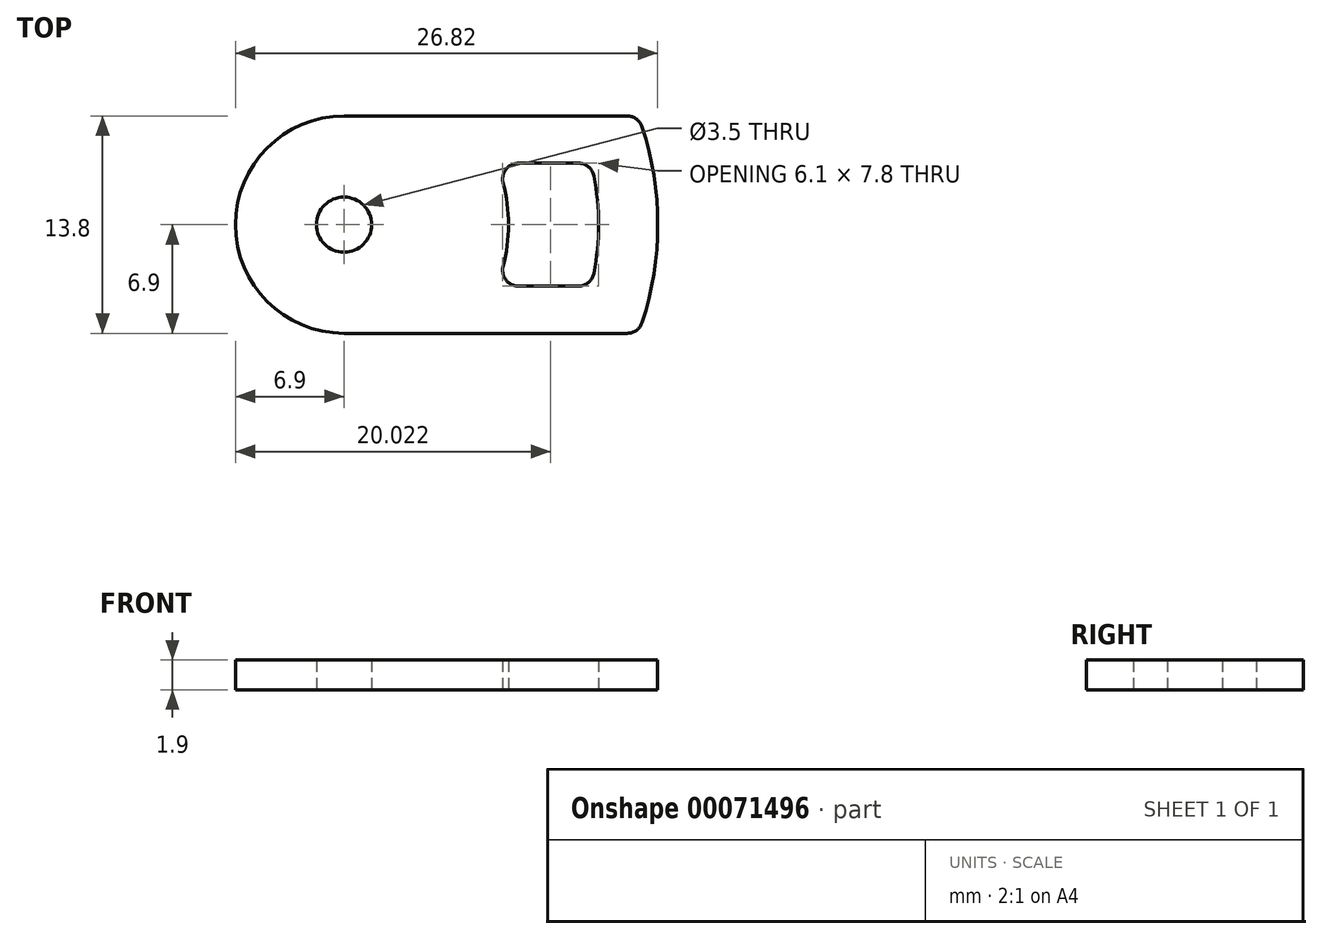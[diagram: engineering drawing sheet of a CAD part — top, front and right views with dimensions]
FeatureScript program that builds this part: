
annotation { "Feature Type Name" : "Feature", "Feature Type Description" : "" }
export const myFeature = defineFeature(function(context is Context, id is Id, definition is map)
    precondition{}
    {
        {
            var Q0;
            Q0=qCreatedBy(makeId("Top.planeOp"),FACE);
            var sketch = newSketch(context, id + "F0", { "sketchPlane" : qUnion([Q0])});
            skCircle(sketch, "E0", {"center": v(0, 0) * mm, "radius": 1.75 * mm});
            skCircle(sketch, "E1", {"center": v(0, 0) * mm, "radius": 6.9 * mm});
            skLineSegment(sketch, "E2", {"start": v(0, 6.9) * mm, "end": v(18.7, 6.9) * mm});
            skLineSegment(sketch, "E3", {"start": v(0, -6.9) * mm, "end": v(18.7, -6.9) * mm});
            skLineSegment(sketch, "E4", {"start": v(9.7, 3.9) * mm, "end": v(15.7, 3.9) * mm});
            skLineSegment(sketch, "E5", {"start": v(15.7, -3.9) * mm, "end": v(9.7, -3.9) * mm});
            skLineSegment(sketch, "E6", {"start": v(9.7, 3.9) * mm, "end": v(5.7, 3.9) * mm, "construction": true});
            skLineSegment(sketch, "E7", {"start": v(5.7, 3.9) * mm, "end": v(5.7, 6.9) * mm, "construction": true});
            skCircle(sketch, "E8", {"center": v(0, 0) * mm, "radius": 10.45 * mm});
            skCircle(sketch, "E9", {"center": v(0, 0) * mm, "radius": 19.92 * mm});
            skCircle(sketch, "E10", {"center": v(0, 0) * mm, "radius": 16.17 * mm});
            skSolve(sketch);
        }
        {
            var Q0;
            Q0=makeQuery(id+"F0.imprint","IMPRINT",FACE,{"disambiguationData":[TD([[makeQuery(id+"F0.imprint","IMPRINT",EDGE,{"derivedFrom":sQuery(id+"F0.wireOp",EDGE,"E0")}),-1.0]])]});
            var Q1;
            {var subQ2=sQuery(id+"F0.wireOp",EDGE,"E2");var subQ5=sQuery(id+"F0.wireOp",EDGE,"E1");var subQ9=makeQuery(id+"F0.imprint","INTERSECT",VERTEX,{"derivedFrom":[subQ5,subQ2]});Q1=makeQuery(id+"F0.imprint","IMPRINT",FACE,{"disambiguationData":[TD([[makeQuery(id+"F0.imprint","IMPRINT",EDGE,{"disambiguationData":[TD([[subQ9,1.0]])],"derivedFrom":subQ5}),-1.0]])]});}
            var Q2;
            {var subQ5=sQuery(id+"F0.wireOp",EDGE,"E4");Q2=makeQuery(id+"F0.imprint","IMPRINT",FACE,{"disambiguationData":[TD([[makeQuery(id+"F0.imprint","IMPRINT",EDGE,{"derivedFrom":subQ5}),1.0]])]});}
            var Q3;
            {var subQ5=sQuery(id+"F0.wireOp",EDGE,"E5");Q3=makeQuery(id+"F0.imprint","IMPRINT",FACE,{"disambiguationData":[TD([[makeQuery(id+"F0.imprint","IMPRINT",EDGE,{"derivedFrom":subQ5}),1.0]])]});}
            var Q4;
            {var subQ2=sQuery(id+"F0.wireOp",EDGE,"E2");var subQ4=sQuery(id+"F0.wireOp",EDGE,"E9");var subQ5=makeQuery(id+"F0.imprint","INTERSECT",VERTEX,{"derivedFrom":[subQ2,subQ4]});Q4=makeQuery(id+"F0.imprint","IMPRINT",FACE,{"disambiguationData":[TD([[makeQuery(id+"F0.imprint","IMPRINT",EDGE,{"disambiguationData":[TD([[subQ5,1.0]])],"derivedFrom":subQ2}),-1.0]])]});}
            extrude(context, id + "F1", {"entities" : qUnion([Q0, Q1, Q2, Q3, Q4]), "depth" : 1.9 * mm});
        }
        {
            var Q0;
            Q0=makeQuery(id+"F1.opExtrude","SWEPT_EDGE",EDGE,{"disambiguationData":[OSD([sQuery(id+"F0.wireOp",EDGE,"E3"),sQuery(id+"F0.wireOp",EDGE,"E9")])]});
            var Q1;
            Q1=makeQuery(id+"F1.opExtrude","SWEPT_EDGE",EDGE,{"disambiguationData":[OSD([sQuery(id+"F0.wireOp",EDGE,"E2"),sQuery(id+"F0.wireOp",EDGE,"E9")])]});
            var Q2;
            Q2=makeQuery(id+"F1.opExtrude","SWEPT_EDGE",EDGE,{"disambiguationData":[OSD([sQuery(id+"F0.wireOp",EDGE,"E4"),sQuery(id+"F0.wireOp",EDGE,"E8")])]});
            var Q3;
            Q3=makeQuery(id+"F1.opExtrude","SWEPT_EDGE",EDGE,{"disambiguationData":[OSD([sQuery(id+"F0.wireOp",EDGE,"E4"),sQuery(id+"F0.wireOp",EDGE,"E10")])]});
            var Q4;
            Q4=makeQuery(id+"F1.opExtrude","SWEPT_EDGE",EDGE,{"disambiguationData":[OSD([sQuery(id+"F0.wireOp",EDGE,"E5"),sQuery(id+"F0.wireOp",EDGE,"E8")])]});
            var Q5;
            Q5=makeQuery(id+"F1.opExtrude","SWEPT_EDGE",EDGE,{"disambiguationData":[OSD([sQuery(id+"F0.wireOp",EDGE,"E5"),sQuery(id+"F0.wireOp",EDGE,"E10")])]});
            fillet(context, id + "F2", {"entities" : qUnion([Q0, Q1, Q2, Q3, Q4, Q5]), "radius" : 1 * mm, "tangentPropagation" : true, "allowEdgeOverflow" : false});
        }
    });
